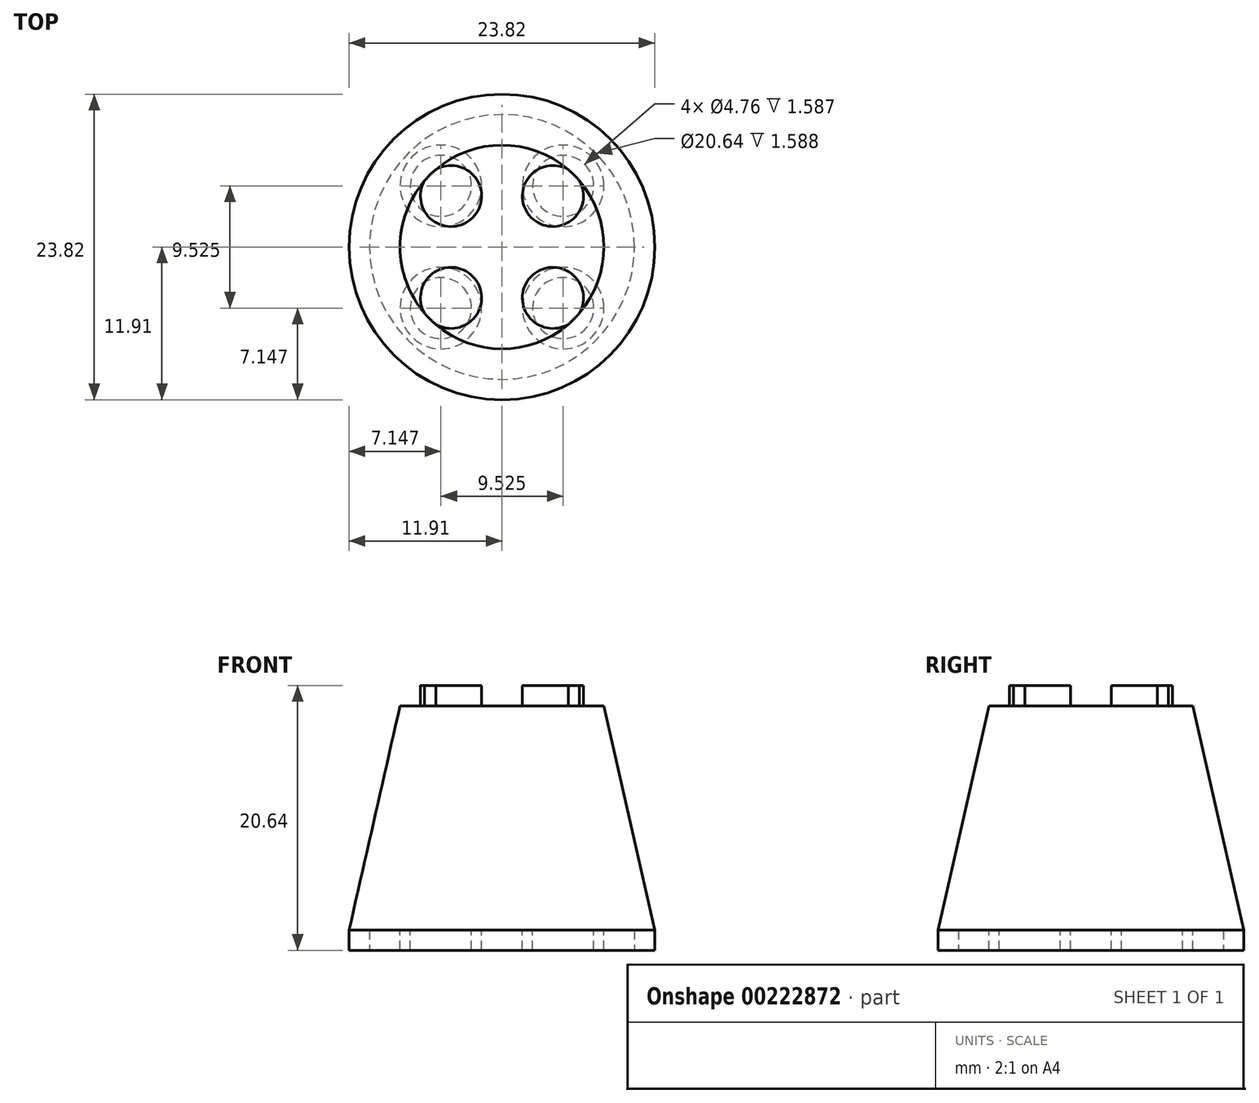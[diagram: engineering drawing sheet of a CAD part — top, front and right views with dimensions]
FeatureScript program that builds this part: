
annotation { "Feature Type Name" : "Feature", "Feature Type Description" : "" }
export const myFeature = defineFeature(function(context is Context, id is Id, definition is map)
    precondition{}
    {
        {
            var Q0;
            Q0=qCreatedBy(makeId("Front.planeOp"),FACE);
            var sketch = newSketch(context, id + "F0", { "sketchPlane" : qUnion([Q0])});
            skLineSegment(sketch, "E0", {"start": v(0, 0) * mm, "end": v(11.9, 0) * mm});
            skLineSegment(sketch, "E1", {"start": v(11.9, 0) * mm, "end": v(11.9, 1.59) * mm});
            skLineSegment(sketch, "E2", {"start": v(0, 0) * mm, "end": v(0, 1.59) * mm});
            skLineSegment(sketch, "E3", {"start": v(0, 1.59) * mm, "end": v(11.9, 1.59) * mm});
            skLineSegment(sketch, "E4", {"start": v(0, 0) * mm, "end": v(0, 19.05) * mm});
            skLineSegment(sketch, "E5", {"start": v(0, 19.05) * mm, "end": v(7.94, 19.05) * mm});
            skLineSegment(sketch, "E6", {"start": v(7.94, 19.05) * mm, "end": v(11.9, 1.59) * mm});
            skLineSegment(sketch, "E7", {"start": v(10.32, 0) * mm, "end": v(10.32, 1.59) * mm});
            skSolve(sketch);
        }
        {
            var Q0;
            {var subQ0=sQuery(id+"F0.wireOp",EDGE,"E1");Q0=makeQuery(id+"F0.imprint","IMPRINT",FACE,{"disambiguationData":[TD([[makeQuery(id+"F0.imprint","IMPRINT",EDGE,{"derivedFrom":subQ0}),1.0]])]});}
            var Q1;
            {var subQ0=sQuery(id+"F0.wireOp",EDGE,"E5");Q1=makeQuery(id+"F0.imprint","IMPRINT",FACE,{"disambiguationData":[TD([[makeQuery(id+"F0.imprint","IMPRINT",EDGE,{"derivedFrom":subQ0}),-1.0]])]});}
            var Q2;
            Q2=sQuery(id+"F0.wireOp",EDGE,"E4");
            revolve(context, id + "F1", {"entities" : qUnion([Q0, Q1]), "axis" : qUnion([Q2]), "revolveType" : RevolveType.FULL});
        }
        {
            var Q0;
            Q0=makeQuery(id+"F1.opRevolve","SWEPT_FACE",FACE,{"disambiguationData":[OSD([sQuery(id+"F0.wireOp",EDGE,"E5")])]});
            var sketch = newSketch(context, id + "F2", { "sketchPlane" : qUnion([Q0])});
            skLineSegment(sketch, "E8", {"start": v(0, 7.94) * mm, "end": v(0, -7.94) * mm});
            skLineSegment(sketch, "E9", {"start": v(-7.94, 0) * mm, "end": v(7.94, 0) * mm});
            skCircle(sketch, "E10", {"center": v(-3.97, -3.97) * mm, "radius": 2.38 * mm});
            skCircle(sketch, "E11.0.1.0", {"center": v(-3.97, 3.97) * mm, "radius": 2.38 * mm});
            skCircle(sketch, "E11.1.0.0", {"center": v(3.97, -3.97) * mm, "radius": 2.38 * mm});
            skCircle(sketch, "E11.1.1.0", {"center": v(3.97, 3.97) * mm, "radius": 2.38 * mm});
            skLineSegment(sketch, "E11.direction1", {"start": v(-3.97, -3.97) * mm, "end": v(3.97, -3.97) * mm, "construction": true});
            skLineSegment(sketch, "E11.direction2", {"start": v(-3.97, -3.97) * mm, "end": v(-3.97, 3.97) * mm, "construction": true});
            skSolve(sketch);
        }
        {
            var Q0;
            {var subQ0=sQuery(id+"F2.wireOp",EDGE,"E10");var subQ1=makeQuery(id+"F1.opRevolve","SWEPT_EDGE",EDGE,{"disambiguationData":[OSD([sQuery(id+"F0.wireOp",EDGE,"E5"),sQuery(id+"F0.wireOp",EDGE,"E6")])]});var subQ2=makeQuery(id+"F2.imprint","INTERSECT",VERTEX,{"disambiguationData":[OD(0.0)],"derivedFrom":[subQ1,subQ0]});Q0=makeQuery(id+"F2.imprint","IMPRINT",FACE,{"disambiguationData":[TD([[makeQuery(id+"F2.imprint","IMPRINT",EDGE,{"disambiguationData":[TD([[subQ2,-1.0]])],"derivedFrom":subQ0}),1.0]])]});}
            var Q1;
            {var subQ0=sQuery(id+"F2.wireOp",EDGE,"E11.0.1.0");var subQ1=makeQuery(id+"F1.opRevolve","SWEPT_EDGE",EDGE,{"disambiguationData":[OSD([sQuery(id+"F0.wireOp",EDGE,"E5"),sQuery(id+"F0.wireOp",EDGE,"E6")])]});var subQ2=makeQuery(id+"F2.imprint","INTERSECT",VERTEX,{"disambiguationData":[OD(0.0)],"derivedFrom":[subQ1,subQ0]});Q1=makeQuery(id+"F2.imprint","IMPRINT",FACE,{"disambiguationData":[TD([[makeQuery(id+"F2.imprint","IMPRINT",EDGE,{"disambiguationData":[TD([[subQ2,1.0]])],"derivedFrom":subQ0}),1.0]])]});}
            var Q2;
            {var subQ0=sQuery(id+"F2.wireOp",EDGE,"E11.1.1.0");var subQ1=makeQuery(id+"F1.opRevolve","SWEPT_EDGE",EDGE,{"disambiguationData":[OSD([sQuery(id+"F0.wireOp",EDGE,"E5"),sQuery(id+"F0.wireOp",EDGE,"E6")])]});var subQ2=makeQuery(id+"F2.imprint","INTERSECT",VERTEX,{"disambiguationData":[OD(0.0)],"derivedFrom":[subQ1,subQ0]});Q2=makeQuery(id+"F2.imprint","IMPRINT",FACE,{"disambiguationData":[TD([[makeQuery(id+"F2.imprint","IMPRINT",EDGE,{"disambiguationData":[TD([[subQ2,-1.0]])],"derivedFrom":subQ0}),1.0]])]});}
            var Q3;
            {var subQ0=sQuery(id+"F2.wireOp",EDGE,"E11.1.0.0");var subQ1=makeQuery(id+"F1.opRevolve","SWEPT_EDGE",EDGE,{"disambiguationData":[OSD([sQuery(id+"F0.wireOp",EDGE,"E5"),sQuery(id+"F0.wireOp",EDGE,"E6")])]});var subQ2=makeQuery(id+"F2.imprint","INTERSECT",VERTEX,{"disambiguationData":[OD(0.0)],"derivedFrom":[subQ1,subQ0]});Q3=makeQuery(id+"F2.imprint","IMPRINT",FACE,{"disambiguationData":[TD([[makeQuery(id+"F2.imprint","IMPRINT",EDGE,{"disambiguationData":[TD([[subQ2,1.0]])],"derivedFrom":subQ0}),1.0]])]});}
            extrude(context, id + "F3", {"entities" : qUnion([Q0, Q1, Q2, Q3]), "operationType" : NewBodyOperationType.ADD, "depth" : 1.59 * mm});
        }
        {
            var Q0;
            Q0=makeQuery(id+"F1.opRevolve","SWEPT_FACE",FACE,{"disambiguationData":[OSD([sQuery(id+"F0.wireOp",EDGE,"E3")])]});
            var sketch = newSketch(context, id + "F4", { "sketchPlane" : qUnion([Q0])});
            skLineSegment(sketch, "E12", {"start": v(0, 10.32) * mm, "end": v(0, -10.32) * mm});
            skLineSegment(sketch, "E13", {"start": v(-10.32, 0) * mm, "end": v(10.32, 0) * mm});
            skCircle(sketch, "E14", {"center": v(-4.76, -4.76) * mm, "radius": 3.18 * mm});
            skCircle(sketch, "E15.0", {"center": v(-4.76, -4.76) * mm, "radius": 2.38 * mm});
            skCircle(sketch, "E16.0.1.0", {"center": v(-4.76, 4.76) * mm, "radius": 3.18 * mm});
            skCircle(sketch, "E16.0.1.1", {"center": v(-4.76, 4.76) * mm, "radius": 2.38 * mm});
            skCircle(sketch, "E16.1.0.0", {"center": v(4.76, -4.76) * mm, "radius": 3.18 * mm});
            skCircle(sketch, "E16.1.0.1", {"center": v(4.76, -4.76) * mm, "radius": 2.38 * mm});
            skCircle(sketch, "E16.1.1.0", {"center": v(4.76, 4.76) * mm, "radius": 3.18 * mm});
            skCircle(sketch, "E16.1.1.1", {"center": v(4.76, 4.76) * mm, "radius": 2.38 * mm});
            skLineSegment(sketch, "E16.direction1", {"start": v(-4.76, -4.76) * mm, "end": v(4.76, -4.76) * mm, "construction": true});
            skLineSegment(sketch, "E16.direction2", {"start": v(-4.76, -4.76) * mm, "end": v(-4.76, 4.76) * mm, "construction": true});
            skSolve(sketch);
        }
        {
            var Q0;
            Q0 = qSketchRegion(id + "F4", true);
            extrude(context, id + "F5", {"entities" : qUnion([Q0]), "operationType" : NewBodyOperationType.ADD, "depth" : 1.59 * mm});
        }
    });
